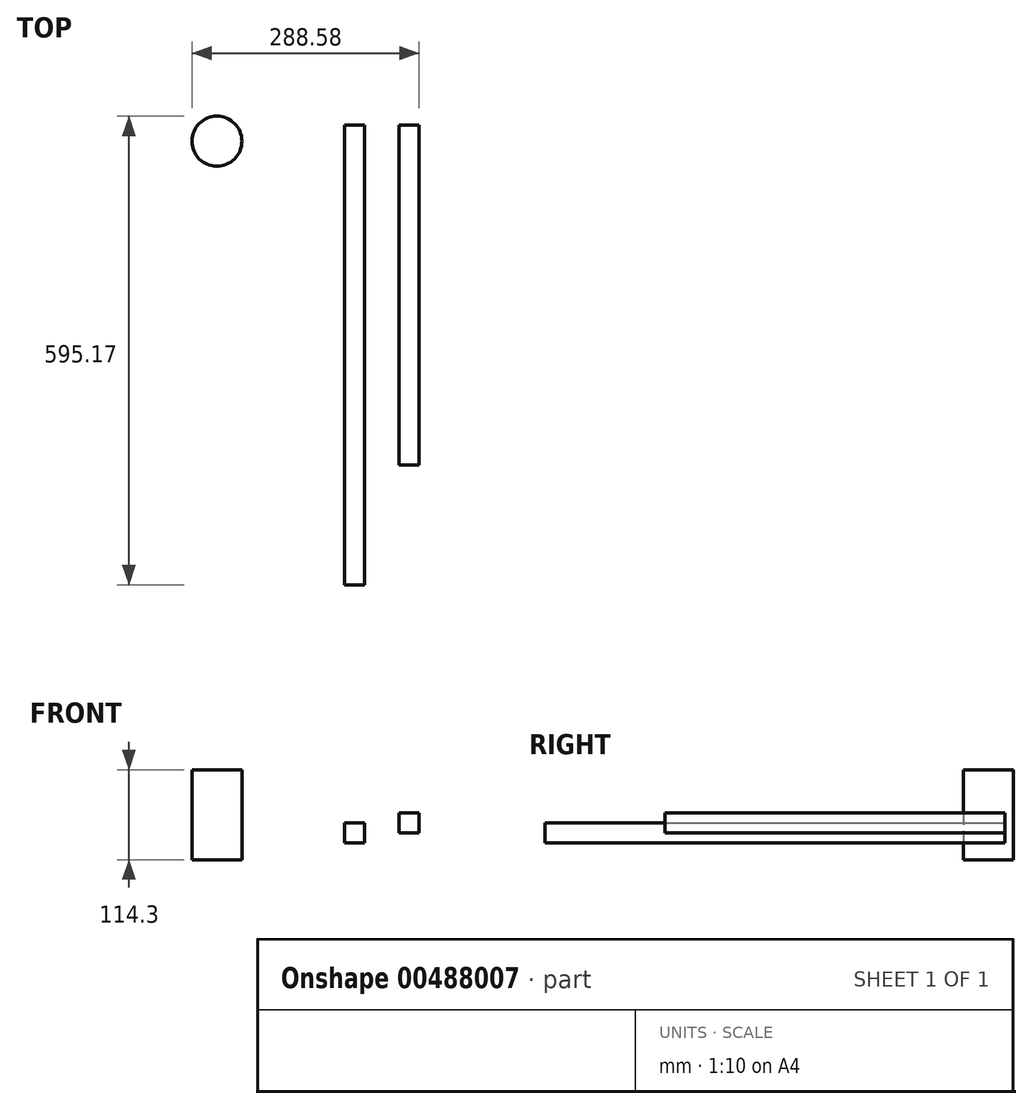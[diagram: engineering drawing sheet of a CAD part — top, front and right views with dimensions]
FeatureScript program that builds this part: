
annotation { "Feature Type Name" : "Feature", "Feature Type Description" : "" }
export const myFeature = defineFeature(function(context is Context, id is Id, definition is map)
    precondition{}
    {
        {
            var Q0;
            Q0=qCreatedBy(makeId("Front.planeOp"),FACE);
            var sketch = newSketch(context, id + "F0", { "sketchPlane" : qUnion([Q0])});
            skLineSegment(sketch, "E0.bottom", {"start": v(-53.6, 46.95) * mm, "end": v(-28.2, 46.95) * mm});
            skLineSegment(sketch, "E0.top", {"start": v(-53.6, 21.55) * mm, "end": v(-28.2, 21.55) * mm});
            skLineSegment(sketch, "E0.left", {"start": v(-53.6, 46.95) * mm, "end": v(-53.6, 21.55) * mm});
            skLineSegment(sketch, "E0.right", {"start": v(-28.2, 46.95) * mm, "end": v(-28.2, 21.55) * mm});
            skSolve(sketch);
        }
        {
            var Q0;
            Q0 = qSketchRegion(id + "F0", true);
            extrude(context, id + "F1", {"entities" : qUnion([Q0]), "depth" : 584.2 * mm});
        }
        {
            var Q0;
            Q0=qCreatedBy(makeId("Front.planeOp"),FACE);
            var sketch = newSketch(context, id + "F2", { "sketchPlane" : qUnion([Q0])});
            skLineSegment(sketch, "E1.bottom", {"start": v(15.67, 59.33) * mm, "end": v(41.07, 59.33) * mm});
            skLineSegment(sketch, "E1.top", {"start": v(15.67, 33.93) * mm, "end": v(41.07, 33.93) * mm});
            skLineSegment(sketch, "E1.left", {"start": v(15.67, 59.33) * mm, "end": v(15.67, 33.93) * mm});
            skLineSegment(sketch, "E1.right", {"start": v(41.07, 59.33) * mm, "end": v(41.07, 33.93) * mm});
            skSolve(sketch);
        }
        {
            var Q0;
            Q0=makeQuery(id+"F2.imprint","IMPRINT",FACE,{"disambiguationData":[TD([[makeQuery(id+"F2.imprint","IMPRINT",EDGE,{"derivedFrom":sQuery(id+"F2.wireOp",EDGE,"E1.bottom")}),-1.0]])]});
            extrude(context, id + "F3", {"entities" : qUnion([Q0]), "depth" : 431.8 * mm});
        }
        {
            var Q0;
            Q0=qCreatedBy(makeId("Top.planeOp"),FACE);
            var sketch = newSketch(context, id + "F4", { "sketchPlane" : qUnion([Q0])});
            skCircle(sketch, "E2", {"center": v(-215.76, -20.78) * mm, "radius": 31.75 * mm});
            skSolve(sketch);
        }
        {
            var Q0;
            Q0 = qSketchRegion(id + "F4", true);
            extrude(context, id + "F5", {"entities" : qUnion([Q0]), "depth" : 114.3 * mm});
        }
    });
